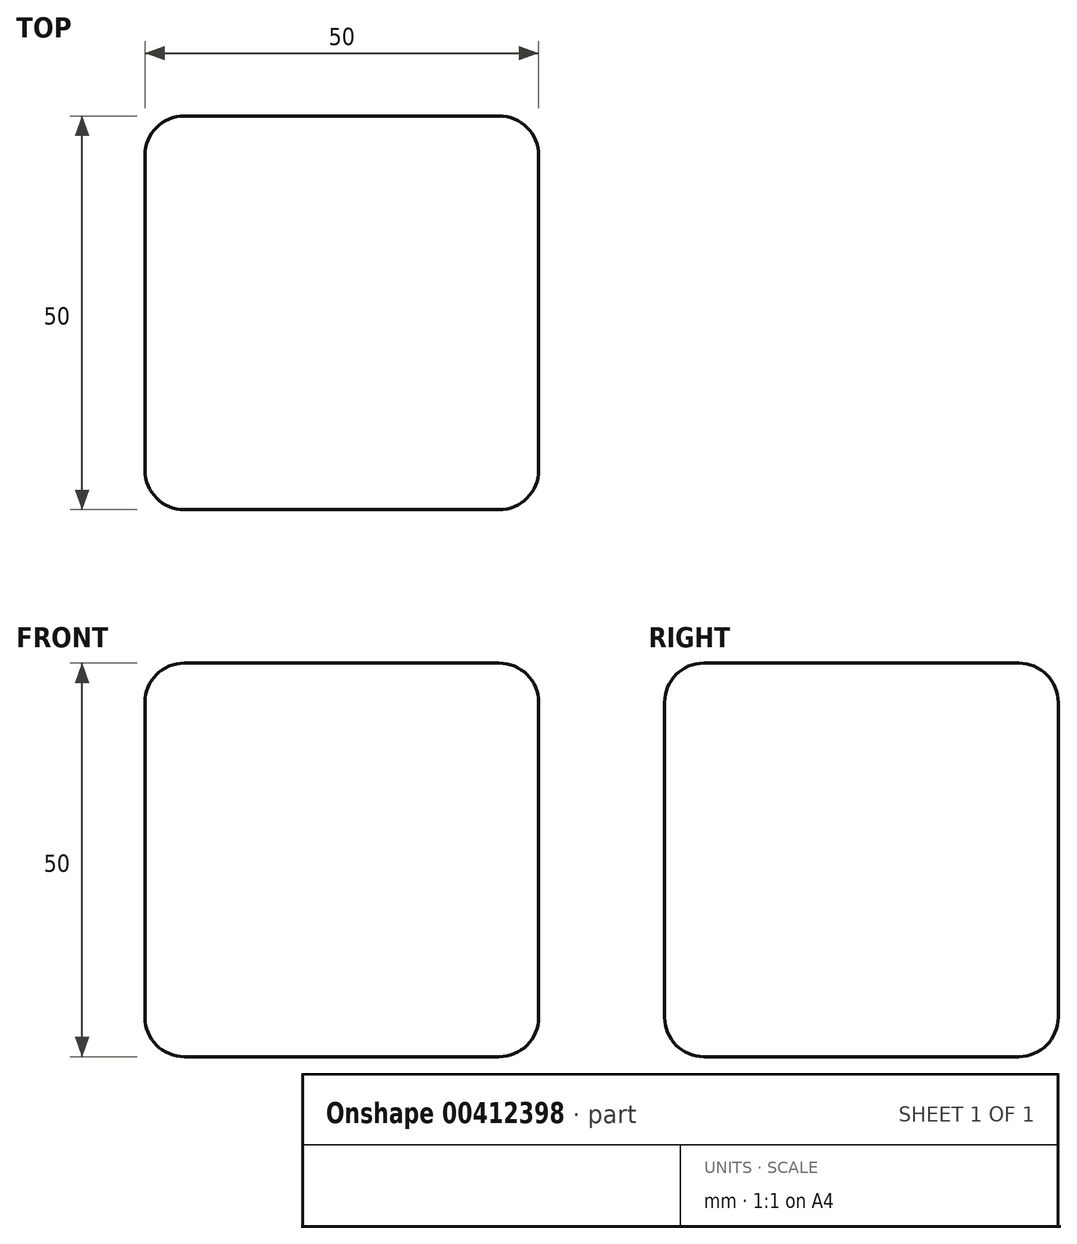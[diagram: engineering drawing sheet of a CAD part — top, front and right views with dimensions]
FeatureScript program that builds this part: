
annotation { "Feature Type Name" : "Feature", "Feature Type Description" : "" }
export const myFeature = defineFeature(function(context is Context, id is Id, definition is map)
    precondition{}
    {
        {
            var Q0;
            Q0=qCreatedBy(makeId("Top.planeOp"),FACE);
            var sketch = newSketch(context, id + "F0", { "sketchPlane" : qUnion([Q0])});
            skLineSegment(sketch, "E0.bottom", {"start": v(-20, 25) * mm, "end": v(20, 25) * mm});
            skLineSegment(sketch, "E0.top", {"start": v(-20, -25) * mm, "end": v(20, -25) * mm});
            skLineSegment(sketch, "E0.left", {"start": v(-25, 20) * mm, "end": v(-25, -20) * mm});
            skLineSegment(sketch, "E0.right", {"start": v(25, 20) * mm, "end": v(25, -20) * mm});
            skPoint(sketch, "E1.visualSharp", {"position": v(-25, 25) * mm});
            skArc(sketch, "E1.filletArc", {"start": v(-20, 25) * mm, "mid": v(-23.54, 23.54) * mm, "end": v(-25, 20) * mm});
            skPoint(sketch, "E2.visualSharp", {"position": v(25, 25) * mm});
            skArc(sketch, "E2.filletArc", {"start": v(25, 20) * mm, "mid": v(23.54, 23.54) * mm, "end": v(20, 25) * mm});
            skPoint(sketch, "E3.visualSharp", {"position": v(25, -25) * mm});
            skArc(sketch, "E3.filletArc", {"start": v(20, -25) * mm, "mid": v(23.54, -23.54) * mm, "end": v(25, -20) * mm});
            skPoint(sketch, "E4.visualSharp", {"position": v(-25, -25) * mm});
            skArc(sketch, "E4.filletArc", {"start": v(-25, -20) * mm, "mid": v(-23.54, -23.54) * mm, "end": v(-20, -25) * mm});
            skSolve(sketch);
        }
        {
            var Q0;
            Q0=makeQuery(id+"F0.imprint","IMPRINT",FACE,{"disambiguationData":[TD([[makeQuery(id+"F0.imprint","IMPRINT",EDGE,{"derivedFrom":sQuery(id+"F0.wireOp",EDGE,"E0.bottom")}),-1.0]])]});
            extrude(context, id + "F1", {"entities" : qUnion([Q0]), "depth" : 50 * mm});
        }
        {
            var Q0;
            Q0=makeQuery(id+"F1.opExtrude","CAP_EDGE",EDGE,{"disambiguationData":[OSD([sQuery(id+"F0.wireOp",EDGE,"E0.right")])],"isStart":false});
            fillet(context, id + "F2", {"entities" : qUnion([Q0]), "radius" : 5 * mm, "tangentPropagation" : true, "allowEdgeOverflow" : false});
        }
        {
            var Q0;
            Q0=makeQuery(id+"F1.opExtrude","CAP_EDGE",EDGE,{"disambiguationData":[OSD([sQuery(id+"F0.wireOp",EDGE,"E0.bottom")])],"isStart":true});
            fillet(context, id + "F3", {"entities" : qUnion([Q0]), "radius" : 5 * mm, "tangentPropagation" : true, "allowEdgeOverflow" : false});
        }
    });
